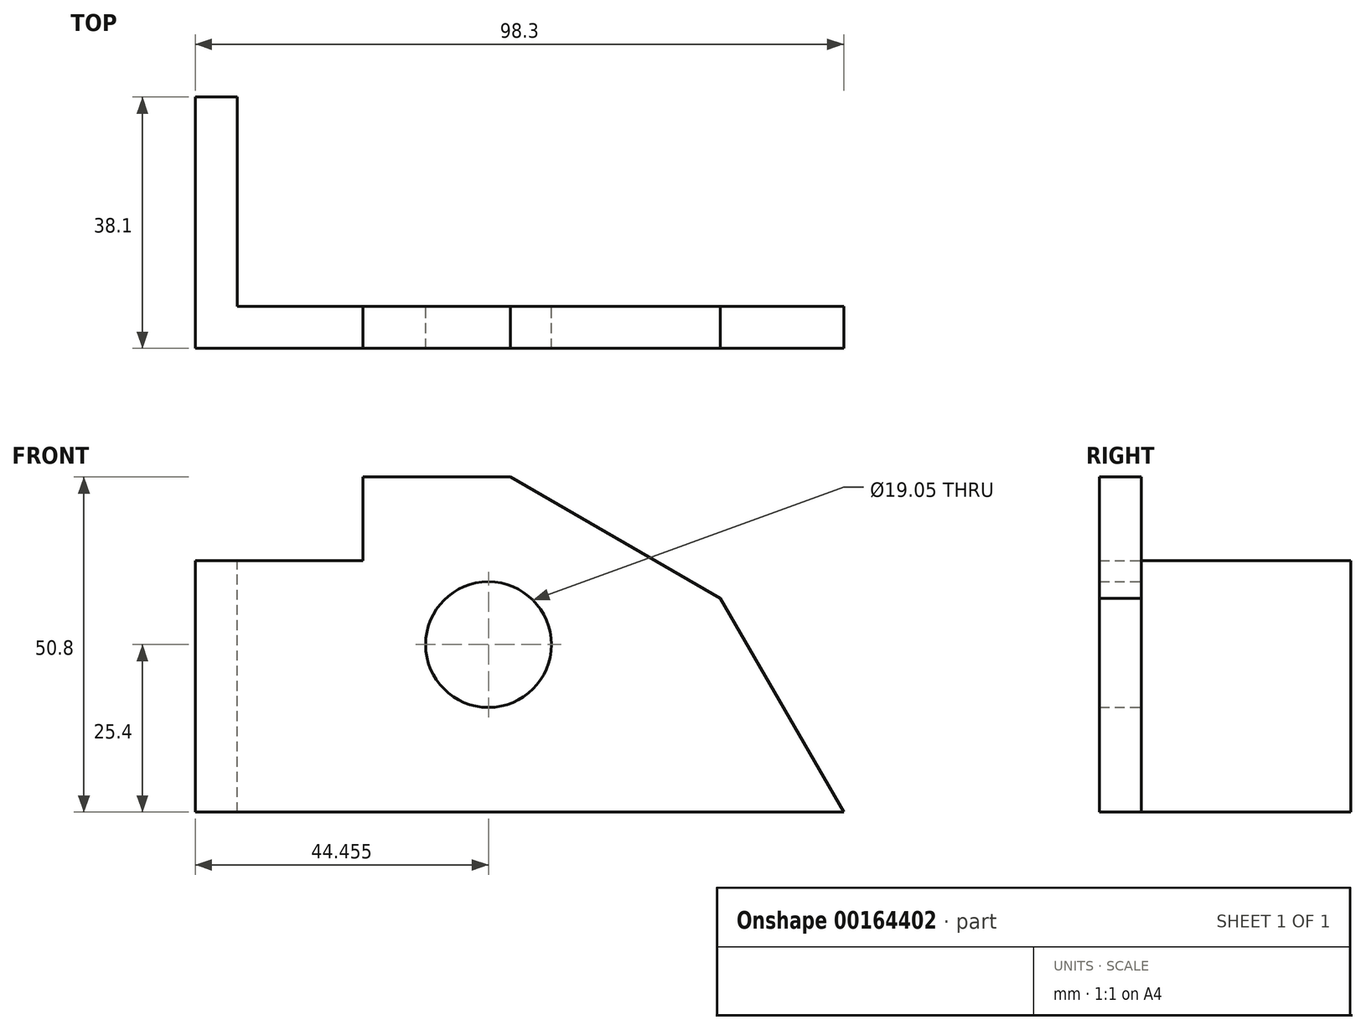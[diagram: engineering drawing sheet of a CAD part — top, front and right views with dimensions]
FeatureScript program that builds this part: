
annotation { "Feature Type Name" : "Feature", "Feature Type Description" : "" }
export const myFeature = defineFeature(function(context is Context, id is Id, definition is map)
    precondition{}
    {
        {
            var Q0;
            Q0=qCreatedBy(makeId("Front.planeOp"),FACE);
            var sketch = newSketch(context, id + "F0", { "sketchPlane" : qUnion([Q0])});
            skLineSegment(sketch, "E0", {"start": v(41.33, -5.52) * mm, "end": v(-50.62, -5.52) * mm});
            skLineSegment(sketch, "E1", {"start": v(-50.62, -5.52) * mm, "end": v(-50.62, 32.58) * mm});
            skLineSegment(sketch, "E2", {"start": v(-50.62, 32.58) * mm, "end": v(-31.57, 32.58) * mm});
            skLineSegment(sketch, "E3", {"start": v(-31.57, 32.58) * mm, "end": v(-31.57, 45.28) * mm});
            skLineSegment(sketch, "E4", {"start": v(-31.57, 45.28) * mm, "end": v(-9.21, 45.28) * mm});
            skLineSegment(sketch, "E5", {"start": v(-9.21, 45.28) * mm, "end": v(22.61, 26.9) * mm});
            skLineSegment(sketch, "E6", {"start": v(22.61, 26.9) * mm, "end": v(41.33, -5.52) * mm});
            skPoint(sketch, "E7", {"position": v(-12.52, 19.88) * mm});
            skCircle(sketch, "E8", {"center": v(-12.52, 19.88) * mm, "radius": 9.53 * mm});
            skSolve(sketch);
        }
        {
            var Q0;
            Q0=makeQuery(id+"F0.imprint","IMPRINT",FACE,{"disambiguationData":[TD([[makeQuery(id+"F0.imprint","IMPRINT",EDGE,{"derivedFrom":sQuery(id+"F0.wireOp",EDGE,"E0")}),-1.0]])]});
            extrude(context, id + "F1", {"entities" : qUnion([Q0]), "depth" : 6.35 * mm});
        }
        {
            var Q0;
            Q0=makeQuery(id+"F1.opExtrude","SWEPT_FACE",FACE,{"disambiguationData":[OSD([sQuery(id+"F0.wireOp",EDGE,"E2")])]});
            var sketch = newSketch(context, id + "F2", { "sketchPlane" : qUnion([Q0])});
            skLineSegment(sketch, "E9", {"start": v(-50.62, -6.35) * mm, "end": v(-56.97, -6.35) * mm});
            skLineSegment(sketch, "E10", {"start": v(-56.97, -6.35) * mm, "end": v(-56.97, 31.75) * mm});
            skLineSegment(sketch, "E11", {"start": v(-56.97, 31.75) * mm, "end": v(-50.62, 31.75) * mm});
            skPoint(sketch, "E11.endSnap0", {"position": v(-50.62, -3.18) * mm});
            skLineSegment(sketch, "E12", {"start": v(-50.62, 31.75) * mm, "end": v(-50.62, -6.35) * mm});
            skSolve(sketch);
        }
        {
            var Q0;
            {var subQ4=sQuery(id+"F2.wireOp",EDGE,"E9");Q0=makeQuery(id+"F2.imprint","IMPRINT",FACE,{"disambiguationData":[TD([[makeQuery(id+"F2.imprint","IMPRINT",EDGE,{"derivedFrom":subQ4}),-1.0]])]});}
            extrude(context, id + "F3", {"entities" : qUnion([Q0]), "operationType" : NewBodyOperationType.ADD, "oppositeDirection" : true, "depth" : 38.1 * mm});
        }
    });
